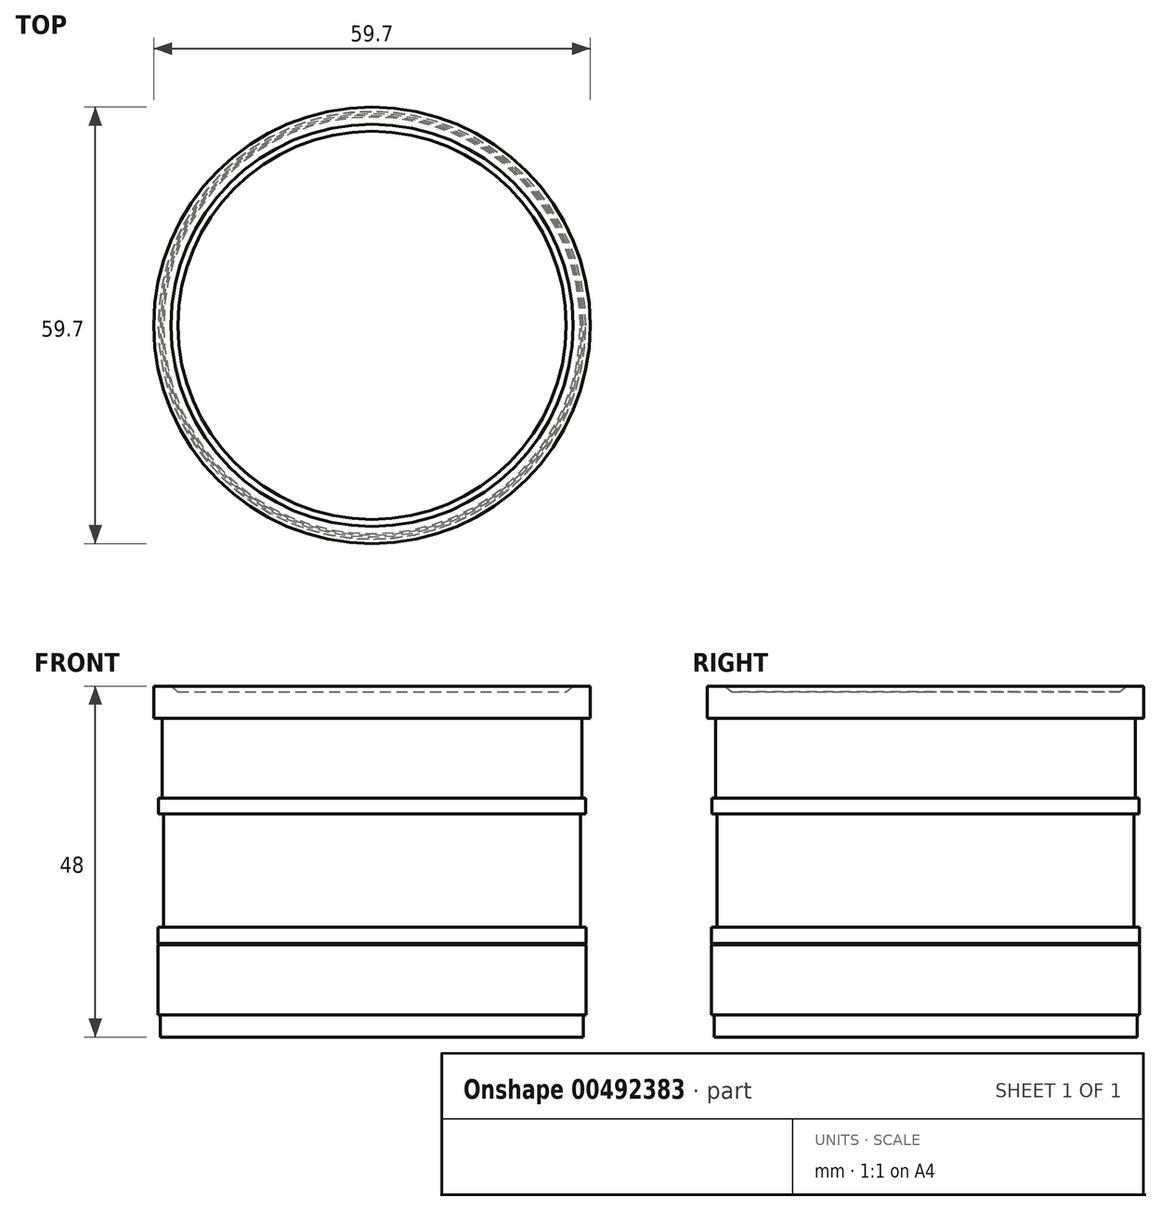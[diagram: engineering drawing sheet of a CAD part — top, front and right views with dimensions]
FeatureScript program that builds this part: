
annotation { "Feature Type Name" : "Feature", "Feature Type Description" : "" }
export const myFeature = defineFeature(function(context is Context, id is Id, definition is map)
    precondition{}
    {
        {
            var Q0;
            Q0=qCreatedBy(makeId("Right.planeOp"),FACE);
            var sketch = newSketch(context, id + "F0", { "sketchPlane" : qUnion([Q0])});
            skLineSegment(sketch, "E0", {"start": v(0, 0) * mm, "end": v(0, 106.9) * mm, "construction": true});
            skLineSegment(sketch, "E1", {"start": v(28.93, 0) * mm, "end": v(28.93, 3) * mm});
            skLineSegment(sketch, "E2", {"start": v(28.93, 3) * mm, "end": v(29.25, 3) * mm});
            skLineSegment(sketch, "E3", {"start": v(29.25, 3) * mm, "end": v(29.25, 12.6) * mm});
            skLineSegment(sketch, "E4", {"start": v(29.25, 12.6) * mm, "end": v(29.2, 12.6) * mm});
            skLineSegment(sketch, "E5", {"start": v(29.2, 12.6) * mm, "end": v(29.2, 12.8) * mm});
            skLineSegment(sketch, "E6", {"start": v(29.2, 12.8) * mm, "end": v(29.25, 12.8) * mm});
            skLineSegment(sketch, "E7", {"start": v(29.25, 12.8) * mm, "end": v(29.25, 15) * mm});
            skLineSegment(sketch, "E8", {"start": v(29.25, 15) * mm, "end": v(28.5, 15) * mm});
            skLineSegment(sketch, "E9", {"start": v(28.5, 15) * mm, "end": v(28.5, 30.5) * mm});
            skLineSegment(sketch, "E10", {"start": v(28.5, 30.5) * mm, "end": v(29.2, 30.5) * mm});
            skLineSegment(sketch, "E11", {"start": v(29.2, 30.5) * mm, "end": v(29.2, 32.7) * mm});
            skLineSegment(sketch, "E12", {"start": v(29.2, 32.7) * mm, "end": v(28.7, 32.7) * mm});
            skLineSegment(sketch, "E13", {"start": v(28.7, 32.7) * mm, "end": v(28.7, 43.6) * mm});
            skLineSegment(sketch, "E14", {"start": v(28.7, 43.6) * mm, "end": v(29.85, 43.6) * mm});
            skLineSegment(sketch, "E15", {"start": v(29.85, 43.6) * mm, "end": v(29.85, 48) * mm});
            skLineSegment(sketch, "E16", {"start": v(29.85, 48) * mm, "end": v(27.5, 48) * mm});
            skLineSegment(sketch, "E17", {"start": v(27.5, 48) * mm, "end": v(26.55, 47.2) * mm});
            skLineSegment(sketch, "E18", {"start": v(26.55, 47.2) * mm, "end": v(26.55, 47.2) * mm});
            skLineSegment(sketch, "E19", {"start": v(26.55, 47.2) * mm, "end": v(0, 47.2) * mm});
            skLineSegment(sketch, "E20", {"start": v(0, 47.2) * mm, "end": v(0, 0) * mm});
            skLineSegment(sketch, "E21", {"start": v(0, 0) * mm, "end": v(28.93, 0) * mm});
            skLineSegment(sketch, "E22", {"start": v(0, 0) * mm, "end": v(26.94, 108.1) * mm, "construction": true});
            skSolve(sketch);
        }
        {
            var Q0;
            Q0=makeQuery(id+"F0.imprint","IMPRINT",FACE,{"disambiguationData":[TD([[makeQuery(id+"F0.imprint","IMPRINT",EDGE,{"derivedFrom":sQuery(id+"F0.wireOp",EDGE,"E1")}),1.0]])]});
            var Q1;
            Q1=sQuery(id+"F0.wireOp",EDGE,"E0");
            revolve(context, id + "F1", {"entities" : qUnion([Q0]), "axis" : qUnion([Q1]), "revolveType" : RevolveType.FULL});
        }
    });
